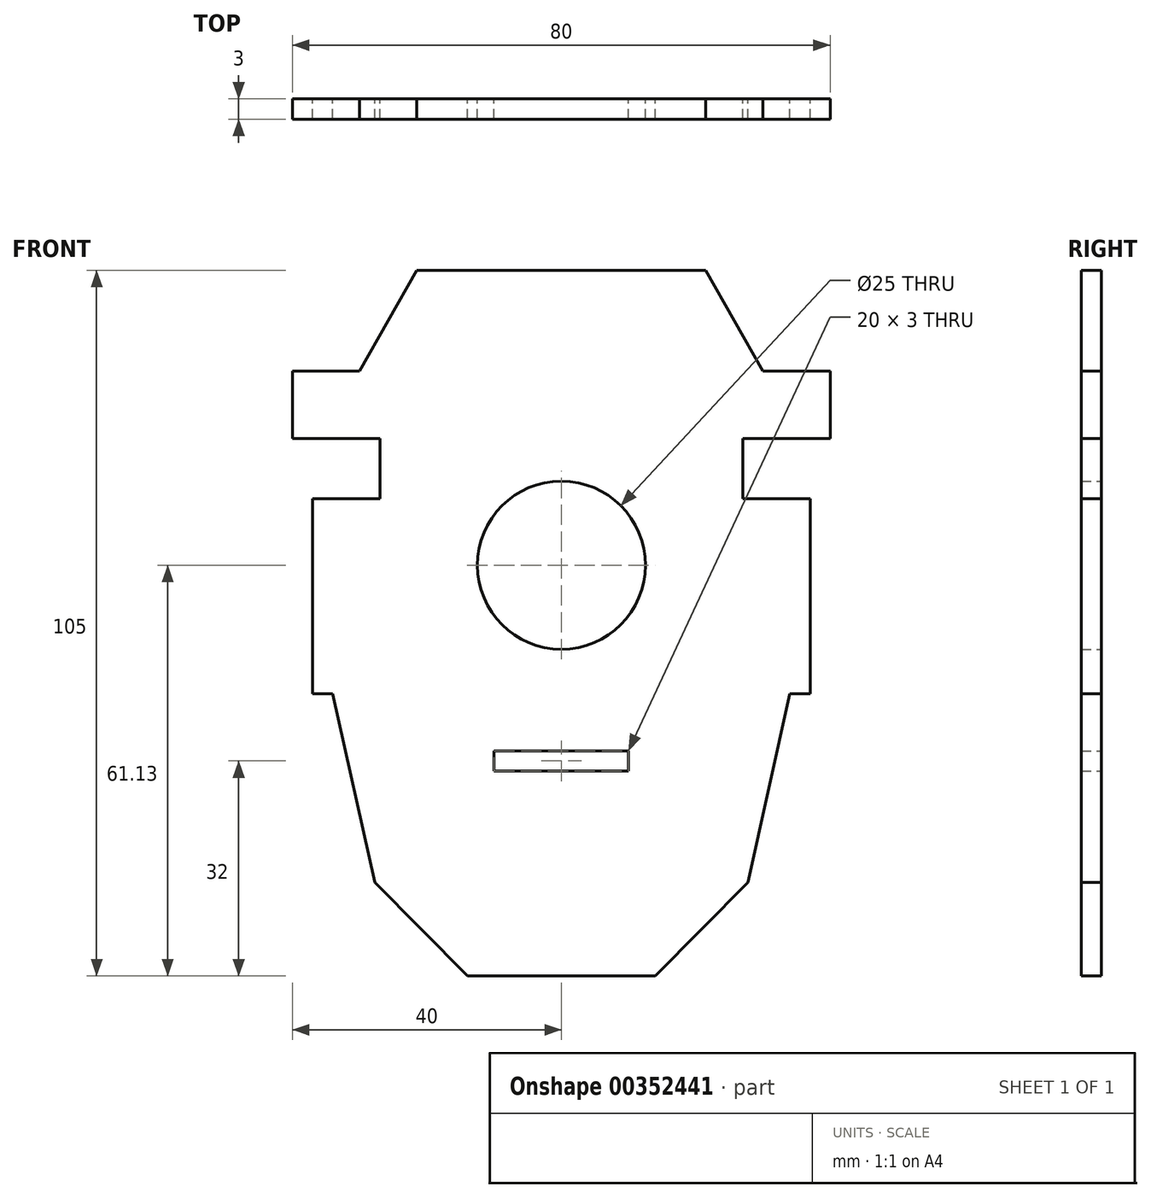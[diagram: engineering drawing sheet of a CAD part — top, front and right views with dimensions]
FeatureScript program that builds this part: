
annotation { "Feature Type Name" : "Feature", "Feature Type Description" : "" }
export const myFeature = defineFeature(function(context is Context, id is Id, definition is map)
    precondition{}
    {
        {
            var Q0;
            Q0=qCreatedBy(makeId("Front.planeOp"),FACE);
            var sketch = newSketch(context, id + "F0", { "sketchPlane" : qUnion([Q0])});
            skLineSegment(sketch, "E0.bottom", {"start": v(21.5, 37.1) * mm, "end": v(-21.5, 37.1) * mm});
            skLineSegment(sketch, "E0.left", {"start": v(40, 22.1) * mm, "end": v(40, 12.1) * mm});
            skLineSegment(sketch, "E0.right", {"start": v(-40, 22.1) * mm, "end": v(-40, 12.1) * mm});
            skPoint(sketch, "E0.middle", {"position": v(0, 0) * mm});
            skLineSegment(sketch, "E1", {"start": v(-40, 22.1) * mm, "end": v(-30, 22.1) * mm});
            skLineSegment(sketch, "E2", {"start": v(-30, 22.1) * mm, "end": v(-21.5, 37.1) * mm});
            skLineSegment(sketch, "E3.MirrorCS", {"start": v(30, 22.1) * mm, "end": v(21.5, 37.1) * mm});
            skLineSegment(sketch, "E4.MirrorCS", {"start": v(40, 22.1) * mm, "end": v(30, 22.1) * mm});
            skLineSegment(sketch, "E5", {"start": v(-27, 12.1) * mm, "end": v(-27, 3.1) * mm});
            skLineSegment(sketch, "E6", {"start": v(-27, 3.1) * mm, "end": v(-37, 3.1) * mm});
            skCircle(sketch, "E7", {"center": v(0, -6.77) * mm, "radius": 12.5 * mm});
            skLineSegment(sketch, "E8.MirrorCS", {"start": v(27, 12.1) * mm, "end": v(27, 3.1) * mm});
            skLineSegment(sketch, "E9.MirrorCS", {"start": v(27, 3.1) * mm, "end": v(37, 3.1) * mm});
            skLineSegment(sketch, "E10", {"start": v(-27, 12.1) * mm, "end": v(-40, 12.1) * mm});
            skLineSegment(sketch, "E11", {"start": v(27, 12.1) * mm, "end": v(40, 12.1) * mm});
            skLineSegment(sketch, "E12.top", {"start": v(-13.96, -70.9) * mm, "end": v(13.96, -70.9) * mm, "construction": true});
            skLineSegment(sketch, "E13", {"start": v(-40, -25.9) * mm, "end": v(-33.48, -55.24) * mm, "construction": true});
            skPoint(sketch, "E14.visualSharp", {"position": v(-30, -70.9) * mm});
            skArc(sketch, "E14.filletArc", {"start": v(-33.48, -55.24) * mm, "mid": v(-26.47, -66.5) * mm, "end": v(-13.96, -70.9) * mm, "construction": true});
            skLineSegment(sketch, "E15.MirrorCS", {"start": v(40, -25.9) * mm, "end": v(33.48, -55.24) * mm, "construction": true});
            skArc(sketch, "E16.MirrorCS", {"start": v(33.48, -55.24) * mm, "mid": v(26.47, -66.5) * mm, "end": v(13.96, -70.9) * mm, "construction": true});
            skPoint(sketch, "E17.orphan", {"position": v(40, -70.9) * mm});
            skLineSegment(sketch, "E18", {"start": v(-40, -25.9) * mm, "end": v(-37, -25.9) * mm, "construction": true});
            skLineSegment(sketch, "E19", {"start": v(-37, -25.9) * mm, "end": v(-37, 3.1) * mm});
            skPoint(sketch, "E20.end.orphan", {"position": v(-40, 3.1) * mm});
            skLineSegment(sketch, "E21.MirrorCS", {"start": v(37, -25.9) * mm, "end": v(37, 3.1) * mm});
            skLineSegment(sketch, "E22.MirrorCS", {"start": v(40, -25.9) * mm, "end": v(37, -25.9) * mm, "construction": true});
            skPoint(sketch, "E23.end.orphan", {"position": v(40, 3.1) * mm});
            skLineSegment(sketch, "E24", {"start": v(-37, -25.9) * mm, "end": v(-34, -25.9) * mm});
            skLineSegment(sketch, "E25", {"start": v(-34, -25.9) * mm, "end": v(-27.76, -53.97) * mm});
            skLineSegment(sketch, "E26", {"start": v(-33.48, -55.24) * mm, "end": v(-27.76, -53.97) * mm, "construction": true});
            skLineSegment(sketch, "E27", {"start": v(-13.96, -70.9) * mm, "end": v(-13.96, -67.9) * mm, "construction": true});
            skLineSegment(sketch, "E28", {"start": v(-13.96, -67.9) * mm, "end": v(13.96, -67.9) * mm});
            skLineSegment(sketch, "E29", {"start": v(13.96, -67.9) * mm, "end": v(13.96, -70.9) * mm, "construction": true});
            skLineSegment(sketch, "E30", {"start": v(-27.76, -53.97) * mm, "end": v(-13.96, -67.9) * mm});
            skLineSegment(sketch, "E31.MirrorCS", {"start": v(-13.96, -67.9) * mm, "end": v(-13.96, -70.9) * mm, "construction": true});
            skLineSegment(sketch, "E32.MirrorCS", {"start": v(13.96, -70.9) * mm, "end": v(-13.96, -70.9) * mm, "construction": true});
            skLineSegment(sketch, "E33.MirrorCS", {"start": v(13.96, -70.9) * mm, "end": v(13.96, -67.9) * mm, "construction": true});
            skLineSegment(sketch, "E34.MirrorCS", {"start": v(33.48, -55.24) * mm, "end": v(27.76, -53.97) * mm, "construction": true});
            skLineSegment(sketch, "E35.MirrorCS", {"start": v(37, -25.9) * mm, "end": v(34, -25.9) * mm});
            skLineSegment(sketch, "E36.MirrorCS", {"start": v(34, -25.9) * mm, "end": v(27.76, -53.97) * mm});
            skLineSegment(sketch, "E37.MirrorCS", {"start": v(27.76, -53.97) * mm, "end": v(13.96, -67.9) * mm});
            skLineSegment(sketch, "E38", {"start": v(-27.76, -53.97) * mm, "end": v(-27.76, -25.9) * mm, "construction": true});
            skLineSegment(sketch, "E39", {"start": v(-27.76, -25.9) * mm, "end": v(-34, -25.9) * mm, "construction": true});
            skLineSegment(sketch, "E40.bottom", {"start": v(-10, -34.4) * mm, "end": v(10, -34.4) * mm});
            skLineSegment(sketch, "E40.top", {"start": v(-10, -37.4) * mm, "end": v(10, -37.4) * mm});
            skLineSegment(sketch, "E40.left", {"start": v(-10, -34.4) * mm, "end": v(-10, -37.4) * mm});
            skLineSegment(sketch, "E40.right", {"start": v(10, -34.4) * mm, "end": v(10, -37.4) * mm});
            skLineSegment(sketch, "E41", {"start": v(-31.44, -37.4) * mm, "end": v(31.44, -37.4) * mm, "construction": true});
            skSolve(sketch);
        }
        {
            var Q0;
            Q0=makeQuery(id+"F0.imprint","IMPRINT",FACE,{"disambiguationData":[TD([[makeQuery(id+"F0.imprint","IMPRINT",EDGE,{"derivedFrom":sQuery(id+"F0.wireOp",EDGE,"E0.bottom")}),1.0]])]});
            extrude(context, id + "F1", {"entities" : qUnion([Q0]), "offsetDistance" : 25 * mm, "depth" : 3 * mm, "symmetric" : true});
        }
    });
